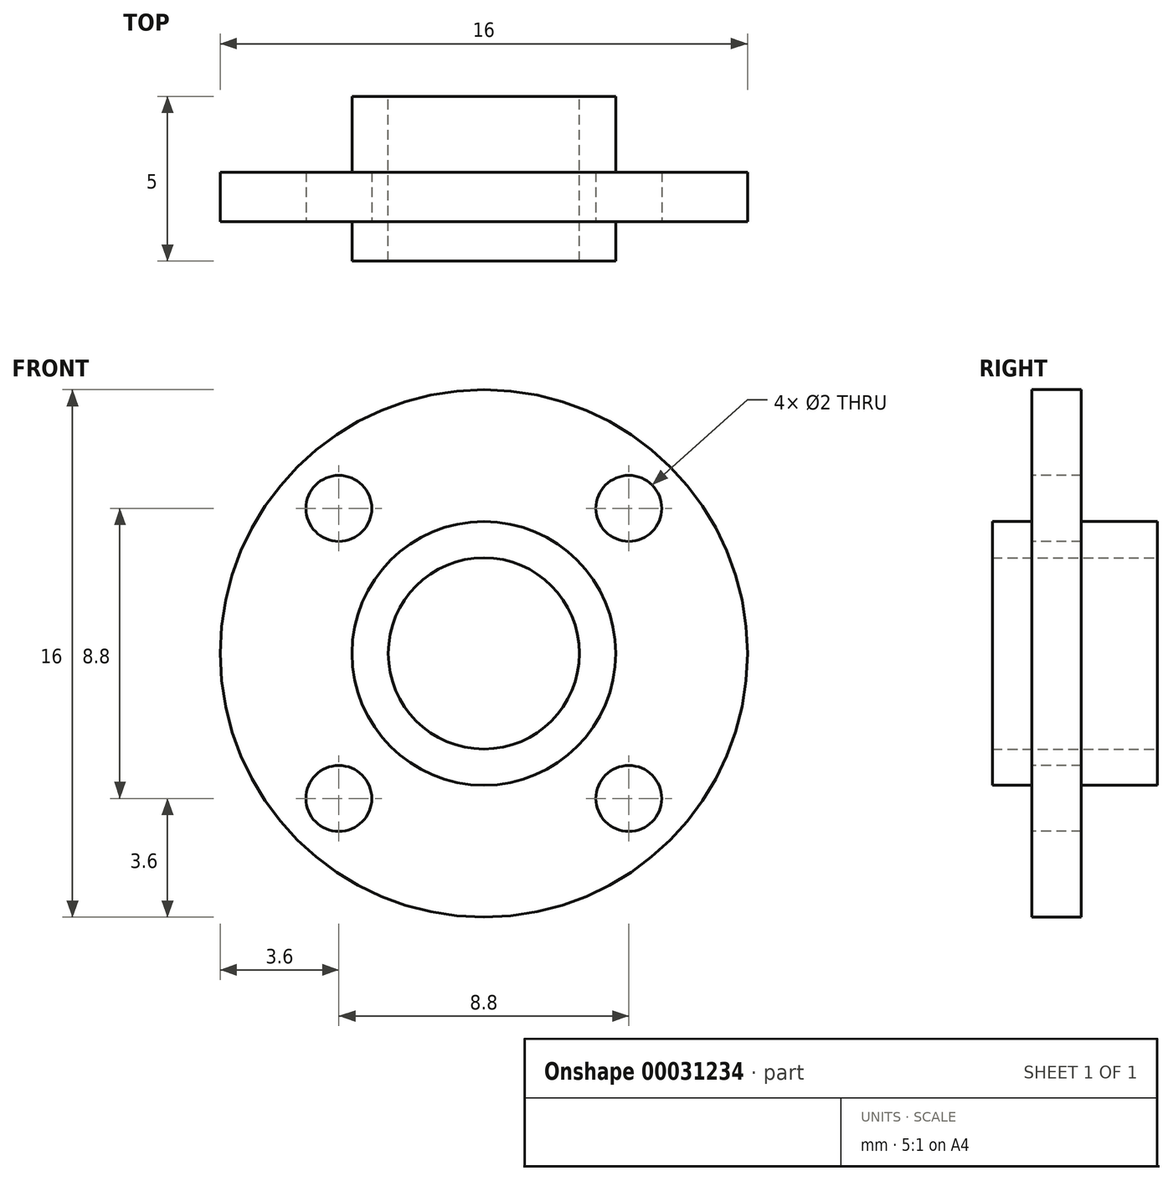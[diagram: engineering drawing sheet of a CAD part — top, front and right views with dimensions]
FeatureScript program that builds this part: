
annotation { "Feature Type Name" : "Feature", "Feature Type Description" : "" }
export const myFeature = defineFeature(function(context is Context, id is Id, definition is map)
    precondition{}
    {
        {
            var Q0;
            Q0=qCreatedBy(makeId("Front.planeOp"),FACE);
            var sketch = newSketch(context, id + "F0", { "sketchPlane" : qUnion([Q0])});
            skCircle(sketch, "E0", {"center": v(0, 0) * mm, "radius": 8 * mm});
            skSolve(sketch);
        }
        {
            var Q0;
            Q0 = qSketchRegion(id + "F0", true);
            extrude(context, id + "F1", {"entities" : qUnion([Q0]), "depth" : 1.5 * mm});
        }
        {
            var Q0;
            Q0=makeQuery(id+"F1.opExtrude","CAP_FACE",FACE,{"disambiguationData":[OSD([sQuery(id+"F0.wireOp",EDGE,"E0")])],"isStart":false});
            var sketch = newSketch(context, id + "F2", { "sketchPlane" : qUnion([Q0])});
            skCircle(sketch, "E1", {"center": v(4.4, 4.4) * mm, "radius": 1 * mm});
            skLineSegment(sketch, "E2", {"start": v(0, 8) * mm, "end": v(0, -8) * mm, "construction": true});
            skLineSegment(sketch, "E3", {"start": v(-8, 0) * mm, "end": v(8, 0) * mm, "construction": true});
            skCircle(sketch, "E4.MirrorC", {"center": v(-4.4, 4.4) * mm, "radius": 1 * mm});
            skCircle(sketch, "E5.MirrorC", {"center": v(-4.4, -4.4) * mm, "radius": 1 * mm});
            skCircle(sketch, "E6.MirrorC", {"center": v(4.4, -4.4) * mm, "radius": 1 * mm});
            skSolve(sketch);
        }
        {
            var Q0;
            Q0=sQuery(id+"F2.wireOp",VERTEX,"E4.MirrorC.center");
            var Q1;
            Q1=sQuery(id+"F2.wireOp",VERTEX,"E1.center");
            var Q2;
            Q2=sQuery(id+"F2.wireOp",VERTEX,"E6.MirrorC.center");
            var Q3;
            Q3=sQuery(id+"F2.wireOp",VERTEX,"E5.MirrorC.center");
            var Q4;
            Q4=makeQuery(id+"F1.opExtrude","SWEPT_BODY",BODY,{"disambiguationData":[OSD([sQuery(id+"F0.wireOp",EDGE,"E0")])]});
            hole(context, id + "F3", {"style" : HoleStyle.SIMPLE, "holeDiameter" : 2 * mm, "endStyle" : HoleEndStyle.THROUGH, "locations" : qUnion([Q0, Q1, Q2, Q3]), "scope" : qUnion([Q4])});
        }
        {
            var Q0;
            Q0=makeQuery(id+"F1.opExtrude","CAP_FACE",FACE,{"disambiguationData":[OSD([sQuery(id+"F0.wireOp",EDGE,"E0")])],"isStart":false});
            var sketch = newSketch(context, id + "F4", { "sketchPlane" : qUnion([Q0])});
            skCircle(sketch, "E7", {"center": v(0, 0) * mm, "radius": 4 * mm});
            skSolve(sketch);
        }
        {
            var Q0;
            Q0 = qSketchRegion(id + "F4", true);
            extrude(context, id + "F5", {"entities" : qUnion([Q0]), "operationType" : NewBodyOperationType.ADD, "depth" : 1.2 * mm});
        }
        {
            var Q0;
            Q0=makeQuery(id+"F1.opExtrude","CAP_FACE",FACE,{"disambiguationData":[OSD([sQuery(id+"F0.wireOp",EDGE,"E0")])],"isStart":true});
            var sketch = newSketch(context, id + "F6", { "sketchPlane" : qUnion([Q0])});
            skCircle(sketch, "E8", {"center": v(0, 0) * mm, "radius": 4 * mm});
            skSolve(sketch);
        }
        {
            var Q0;
            Q0 = qSketchRegion(id + "F6", true);
            extrude(context, id + "F7", {"entities" : qUnion([Q0]), "operationType" : NewBodyOperationType.ADD, "depth" : 2.3 * mm});
        }
        {
            var Q0;
            Q0=makeQuery(id+"F7.opExtrude","CAP_FACE",FACE,{"disambiguationData":[OSD([sQuery(id+"F6.wireOp",EDGE,"E8")])],"isStart":false});
            var sketch = newSketch(context, id + "F8", { "sketchPlane" : qUnion([Q0])});
            skCircle(sketch, "E9", {"center": v(0, 0) * mm, "radius": 2.9 * mm});
            skSolve(sketch);
        }
        {
            var Q0;
            Q0=sQuery(id+"F8.wireOp",VERTEX,"E9.center");
            var Q1;
            Q1=makeQuery(id+"F1.opExtrude","SWEPT_BODY",BODY,{"disambiguationData":[OSD([sQuery(id+"F0.wireOp",EDGE,"E0")])]});
            hole(context, id + "F9", {"style" : HoleStyle.SIMPLE, "holeDiameter" : 5.8 * mm, "endStyle" : HoleEndStyle.THROUGH, "locations" : qUnion([Q0]), "scope" : qUnion([Q1])});
        }
    });
